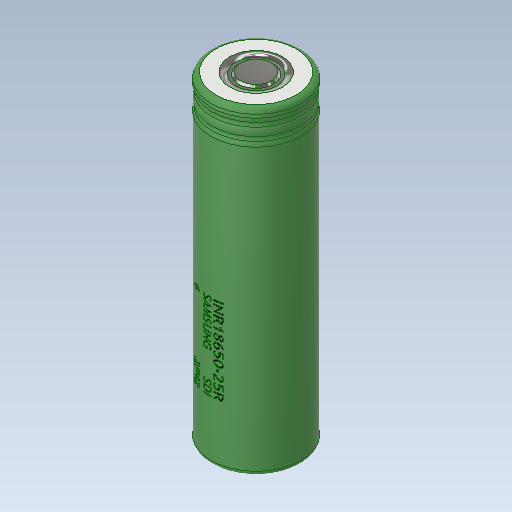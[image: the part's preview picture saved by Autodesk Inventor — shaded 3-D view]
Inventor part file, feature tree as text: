
AUTODESK INVENTOR PART (.ipt)
format: ipt  version: 2020.1 (Build 241239000, 239)  size: 1,017,856 bytes
history: native  units: mm
features: fillet x3, sketch x3, revolve x2, plane x1, emboss x1, chamfer x1
ambient origin geometry x8: Origin, YZ Plane, XZ Plane, XY Plane, X Axis, Y Axis, Z Axis, Center Point
bodies: Solid1 (feature_tree)
feature tree (11):
  revolve  "Revolution1"  [1 undecoded]
  fillet  "Fillet1"  [1 undecoded]
  plane  "Work Plane1"
  emboss  "Emboss2"
  revolve  "Revolution2"  [1 undecoded]
  chamfer  "Chamfer1"  Distance=20.0mm
  fillet  "Fillet4"  Radius=0.01mm
  fillet  "Fillet5"  Radius=3.5mm
  sketch  "Sketch1"  dims[d0=65.0mm d1=9.165mm d2=90.0deg]
  sketch  "Sketch4"  dims[d3=1.0mm d18=0.5mm]
  sketch  "Sketch6"  dims[d19=7.0mm d20=20.0mm d21=0.01mm d22=0.174533mm d23=3.5mm d27=0.7mm d28=2.5mm d29=0.0mm d30=6.0mm d31=90.0deg d32=0.4mm d33=0.4mm d34=0.5mm d35=45.0deg d36=1.0mm d37=2.0mm d38=2.0mm d39=10.0mm d40=0.0mm]
note: 3 required parameter values undecoded (feature->parameter linkage not recoverable at this tier; creation-order binding heuristic only, values carry confidence <= 0.55)